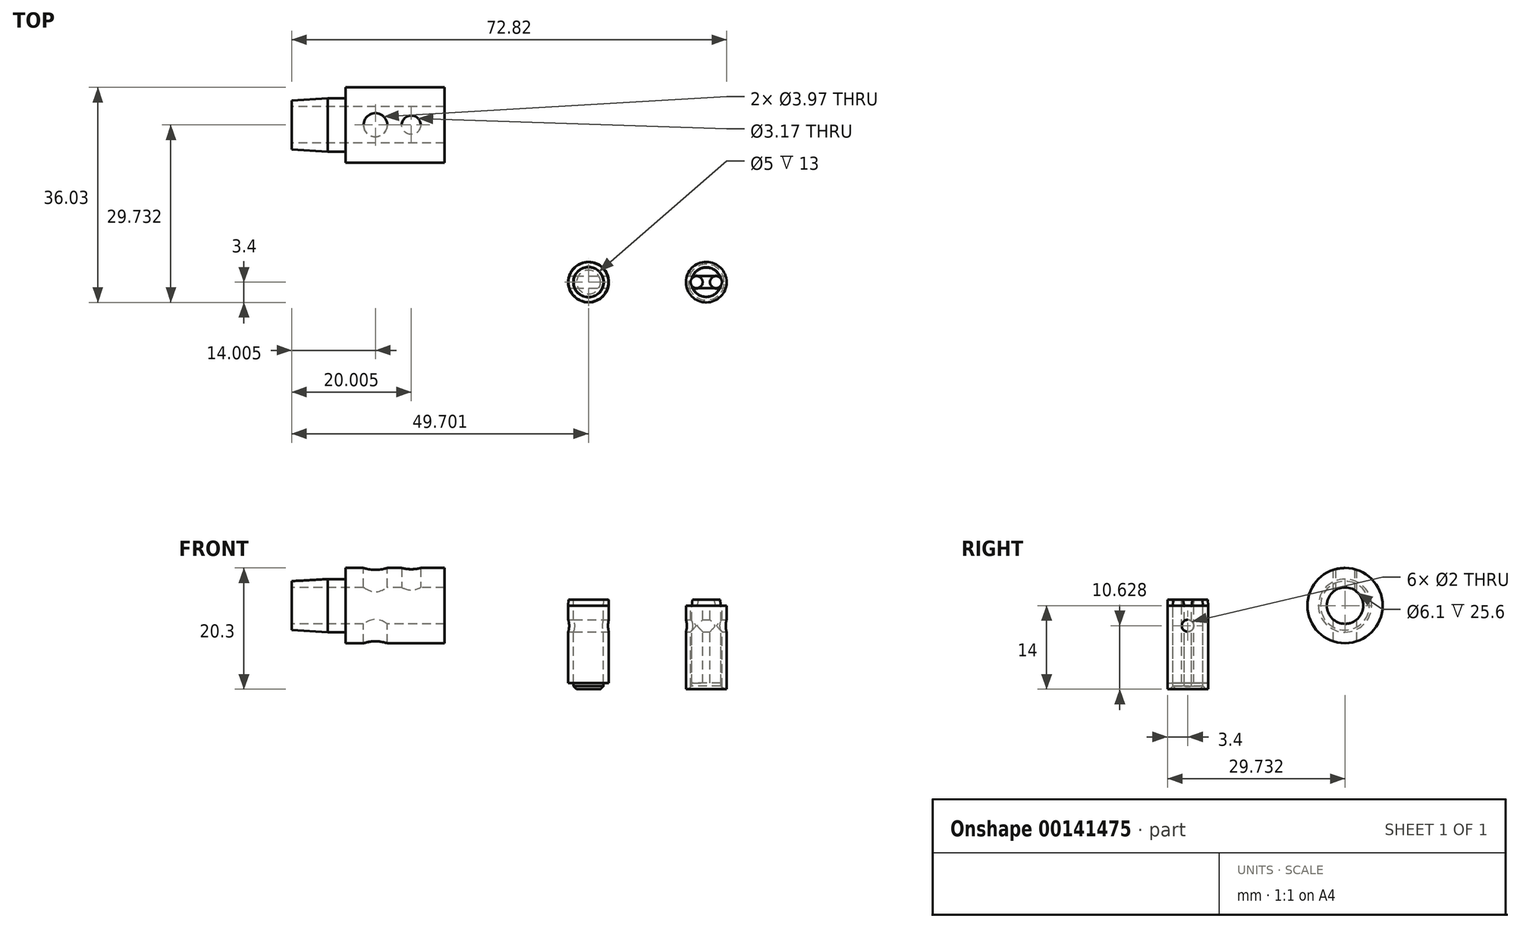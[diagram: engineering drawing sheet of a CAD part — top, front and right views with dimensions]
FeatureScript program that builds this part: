
annotation { "Feature Type Name" : "Feature", "Feature Type Description" : "" }
export const myFeature = defineFeature(function(context is Context, id is Id, definition is map)
    precondition{}
    {
        {
            var Q0;
            Q0=qCreatedBy(makeId("Top.planeOp"),FACE);
            var sketch = newSketch(context, id + "F0", { "sketchPlane" : qUnion([Q0])});
            skCircle(sketch, "E0", {"center": v(0, 0) * mm, "radius": 3.4 * mm});
            skCircle(sketch, "E1", {"center": v(0, 0) * mm, "radius": 2.5 * mm});
            skLineSegment(sketch, "E2", {"start": v(-9.86, 9.58) * mm, "end": v(-9.86, -9.58) * mm, "construction": true});
            skCircle(sketch, "E3.MirrorC", {"center": v(-19.72, 0) * mm, "radius": 2.5 * mm});
            skCircle(sketch, "E4.MirrorC", {"center": v(-19.72, 0) * mm, "radius": 3.4 * mm});
            skCircle(sketch, "E5", {"center": v(1.62, 0) * mm, "radius": 1.01 * mm});
            skLineSegment(sketch, "E6", {"start": v(0, 0) * mm, "end": v(0, 2.5) * mm, "construction": true});
            skCircle(sketch, "E7.MirrorC", {"center": v(-1.62, 0) * mm, "radius": 1.01 * mm});
            skLineSegment(sketch, "E8", {"start": v(-1.62, 1.01) * mm, "end": v(1.62, 1.01) * mm});
            skLineSegment(sketch, "E9", {"start": v(1.62, 1.01) * mm, "end": v(1.62, -1.01) * mm});
            skLineSegment(sketch, "E10", {"start": v(1.62, -1.01) * mm, "end": v(-1.62, -1.01) * mm});
            skLineSegment(sketch, "E11", {"start": v(-1.62, -1.01) * mm, "end": v(-1.62, 1.01) * mm});
            skCircle(sketch, "E12.MirrorC", {"center": v(-21.34, 0) * mm, "radius": 1.01 * mm});
            skSolve(sketch);
        }
        {
            var Q0;
            Q0=makeQuery(id+"F0.imprint","IMPRINT",FACE,{"disambiguationData":[TD([[makeQuery(id+"F0.imprint","IMPRINT",EDGE,{"derivedFrom":sQuery(id+"F0.wireOp",EDGE,"E0")}),1.0]])]});
            var Q1;
            Q1=makeQuery(id+"F0.imprint","IMPRINT",FACE,{"disambiguationData":[TD([[makeQuery(id+"F0.imprint","IMPRINT",EDGE,{"derivedFrom":sQuery(id+"F0.wireOp",EDGE,"E3.MirrorC")}),1.0]])]});
            var Q2;
            Q2=sQuery(id+"F0.wireOp",EDGE,"E0");
            extrude(context, id + "F1", {"entities" : qUnion([Q0, Q1]), "surfaceEntities" : qUnion([Q2]), "oppositeDirection" : true, "depth" : 14 * mm});
        }
        {
            var Q0;
            {var subQ0=sQuery(id+"F0.wireOp",EDGE,"E11");Q0=makeQuery(id+"F0.imprint","IMPRINT",FACE,{"disambiguationData":[TD([[makeQuery(id+"F0.imprint","IMPRINT",EDGE,{"derivedFrom":subQ0}),-1.0]])]});}
            var Q1;
            {var subQ4=sQuery(id+"F0.wireOp",EDGE,"E11");Q1=makeQuery(id+"F0.imprint","IMPRINT",FACE,{"disambiguationData":[TD([[makeQuery(id+"F0.imprint","IMPRINT",EDGE,{"derivedFrom":subQ4}),1.0]])]});}
            var Q2;
            {var subQ0=sQuery(id+"F0.wireOp",EDGE,"E9");Q2=makeQuery(id+"F0.imprint","IMPRINT",FACE,{"disambiguationData":[TD([[makeQuery(id+"F0.imprint","IMPRINT",EDGE,{"derivedFrom":subQ0}),-1.0]])]});}
            var Q3;
            {var subQ4=sQuery(id+"F0.wireOp",EDGE,"E9");Q3=makeQuery(id+"F0.imprint","IMPRINT",FACE,{"disambiguationData":[TD([[makeQuery(id+"F0.imprint","IMPRINT",EDGE,{"derivedFrom":subQ4}),1.0]])]});}
            extrude(context, id + "F2", {"entities" : qUnion([Q0, Q1, Q2, Q3]), "operationType" : NewBodyOperationType.REMOVE, "oppositeDirection" : true, "depth" : 15 * mm, "hasSecondDirection" : true, "secondDirectionOppositeDirection" : false, "secondDirectionDepth" : 5 * mm});
        }
        {
            var Q0;
            {var subQ5=sQuery(id+"F0.wireOp",EDGE,"E8");Q0=makeQuery(id+"F0.imprint","IMPRINT",FACE,{"disambiguationData":[TD([[makeQuery(id+"F0.imprint","IMPRINT",EDGE,{"derivedFrom":subQ5}),1.0]])]});}
            var Q1;
            {var subQ5=sQuery(id+"F0.wireOp",EDGE,"E10");Q1=makeQuery(id+"F0.imprint","IMPRINT",FACE,{"disambiguationData":[TD([[makeQuery(id+"F0.imprint","IMPRINT",EDGE,{"derivedFrom":subQ5}),1.0]])]});}
            var Q2;
            {var subQ0=sQuery(id+"F0.wireOp",EDGE,"E12.MirrorC");var subQ1=sQuery(id+"F0.wireOp",EDGE,"E3.MirrorC");var subQ2=makeQuery(id+"F0.imprint","INTERSECT",VERTEX,{"disambiguationData":[OD(0.0)],"derivedFrom":[subQ1,subQ0]});Q2=makeQuery(id+"F0.imprint","IMPRINT",FACE,{"disambiguationData":[TD([[makeQuery(id+"F0.imprint","IMPRINT",EDGE,{"disambiguationData":[TD([[subQ2,1.0]])],"derivedFrom":subQ1}),-1.0]])]});}
            var Q3;
            {var subQ0=sQuery(id+"F0.wireOp",EDGE,"E12.MirrorC");var subQ1=sQuery(id+"F0.wireOp",EDGE,"E3.MirrorC");var subQ2=makeQuery(id+"F0.imprint","INTERSECT",VERTEX,{"disambiguationData":[OD(0.0)],"derivedFrom":[subQ1,subQ0]});Q3=makeQuery(id+"F0.imprint","IMPRINT",FACE,{"disambiguationData":[TD([[makeQuery(id+"F0.imprint","IMPRINT",EDGE,{"disambiguationData":[TD([[subQ2,-1.0]])],"derivedFrom":subQ1}),-1.0]])]});}
            var Q4;
            {var subQ1=sQuery(id+"F0.wireOp",EDGE,"E8");Q4=makeQuery(id+"F0.imprint","IMPRINT",FACE,{"disambiguationData":[TD([[makeQuery(id+"F0.imprint","IMPRINT",EDGE,{"derivedFrom":subQ1}),-1.0]])]});}
            var Q5;
            Q5=sQuery(id+"F0.wireOp",EDGE,"E1");
            var Q6;
            Q6=makeQuery(id+"F1.opExtrude","CAP_FACE",FACE,{"disambiguationData":[OSD([sQuery(id+"F0.wireOp",EDGE,"E3.MirrorC"),sQuery(id+"F0.wireOp",EDGE,"E4.MirrorC")])],"isStart":false});
            extrude(context, id + "F3", {"entities" : qUnion([Q0, Q1, Q2, Q3, Q4]), "surfaceEntities" : qUnion([Q5]), "oppositeDirection" : true, "endBoundEntityFace" : qUnion([Q6]), "depth" : 13 * mm, "hasSecondDirection" : true, "secondDirectionOppositeDirection" : false, "secondDirectionDepth" : 1 * mm, "hasSecondDirectionDraft" : true, "secondDirectionDraftAngle" : 3 * degree, "secondDirectionDraftPullDirection" : true});
        }
        {
            var Q0;
            {var subQ0=sQuery(id+"F0.wireOp",EDGE,"E8");var subQ1=sQuery(id+"F0.wireOp",EDGE,"E5");var subQ2=makeQuery(id+"F0.imprint","INTERSECT",VERTEX,{"derivedFrom":[subQ1,subQ0]});Q0=makeQuery(id+"F0.imprint","IMPRINT",FACE,{"disambiguationData":[TD([[makeQuery(id+"F0.imprint","IMPRINT",EDGE,{"disambiguationData":[TD([[subQ2,-1.0]])],"derivedFrom":subQ1}),-1.0]])]});}
            extrude(context, id + "F4", {"entities" : qUnion([Q0]), "operationType" : NewBodyOperationType.REMOVE, "depth" : 2 * mm});
        }
        {
            var Q0;
            Q0=makeQuery(id+"F1.opExtrude","CAP_EDGE",EDGE,{"disambiguationData":[OSD([sQuery(id+"F0.wireOp",EDGE,"E1")])],"isStart":false});
            var Q1;
            Q1=makeQuery(id+"F1.opExtrude","CAP_EDGE",EDGE,{"disambiguationData":[OSD([sQuery(id+"F0.wireOp",EDGE,"E3.MirrorC")])],"isStart":false});
            chamfer(context, id + "F5", {"entities" : qUnion([Q0, Q1]), "width" : .5 * mm, "tangentPropagation" : true});
        }
        {
            var Q0;
            Q0=qCreatedBy(makeId("Right.planeOp"),FACE);
            cPlane(context, id + "F6", {"entities" : qUnion([Q0]), "cplaneType" : CPlaneType.OFFSET, "offset" : 25 * mm, "width" : 150 * mm, "height" : 150 * mm});
        }
        {
            var Q0;
            Q0=qCreatedBy(id+"F6.planeOp",FACE);
            var sketch = newSketch(context, id + "F7", { "sketchPlane" : qUnion([Q0])});
            skCircle(sketch, "E13", {"center": v(0, -3.37) * mm, "radius": 1 * mm});
            skSolve(sketch);
        }
        {
            var Q0;
            Q0 = qSketchRegion(id + "F7", true);
            extrude(context, id + "F8", {"entities" : qUnion([Q0]), "operationType" : NewBodyOperationType.REMOVE, "oppositeDirection" : true, "depth" : 100 * mm});
        }
        {
            var Q0;
            Q0=qCreatedBy(makeId("Top.planeOp"),FACE);
            var sketch = newSketch(context, id + "F9", { "sketchPlane" : qUnion([Q0])});
            skLineSegment(sketch, "E14", {"start": v(-55.42, 26.33) * mm, "end": v(-48.93, 26.33) * mm, "construction": true});
            skLineSegment(sketch, "E15", {"start": v(-60.42, 30.78) * mm, "end": v(-60.42, 32.63) * mm});
            skLineSegment(sketch, "E16", {"start": v(-60.42, 32.63) * mm, "end": v(-43.82, 32.63) * mm});
            skLineSegment(sketch, "E17", {"start": v(-69.42, 29.38) * mm, "end": v(-43.82, 29.38) * mm});
            skCircle(sketch, "E18", {"center": v(-49.42, 26.33) * mm, "radius": 1.59 * mm});
            skCircle(sketch, "E19", {"center": v(-55.42, 26.33) * mm, "radius": 1.98 * mm});
            skLineSegment(sketch, "E20", {"start": v(-55.42, 26.33) * mm, "end": v(-77.02, 26.33) * mm});
            skPoint(sketch, "E21", {"position": v(-63.42, 30.78) * mm});
            skCircle(sketch, "E22", {"center": v(-49.42, 26.33) * mm, "radius": 1.98 * mm});
            skLineSegment(sketch, "E23", {"start": v(-69.42, 30.43) * mm, "end": v(-69.42, 29.38) * mm});
            skLineSegment(sketch, "E24", {"start": v(-43.82, 32.63) * mm, "end": v(-43.82, 29.38) * mm});
            skLineSegment(sketch, "E25", {"start": v(-63.42, 30.78) * mm, "end": v(-60.42, 30.78) * mm});
            skLineSegment(sketch, "E26", {"start": v(-69.42, 30.43) * mm, "end": v(-63.42, 30.78) * mm});
            skLineSegment(sketch, "E27.MirrorCS", {"start": v(-69.42, 23.28) * mm, "end": v(-43.82, 23.28) * mm});
            skLineSegment(sketch, "E28.MirrorCS", {"start": v(-60.42, 20.03) * mm, "end": v(-43.82, 20.03) * mm});
            skLineSegment(sketch, "E29.MirrorCS", {"start": v(-43.82, 20.03) * mm, "end": v(-43.82, 23.28) * mm});
            skLineSegment(sketch, "E30.MirrorCS", {"start": v(-60.42, 21.88) * mm, "end": v(-60.42, 20.03) * mm});
            skLineSegment(sketch, "E31.MirrorCS", {"start": v(-63.42, 21.88) * mm, "end": v(-60.42, 21.88) * mm});
            skLineSegment(sketch, "E32.MirrorCS", {"start": v(-69.42, 22.24) * mm, "end": v(-63.42, 21.88) * mm});
            skLineSegment(sketch, "E33.MirrorCS", {"start": v(-69.42, 22.24) * mm, "end": v(-69.42, 23.28) * mm});
            skSolve(sketch);
        }
        {
            var Q0;
            Q0=makeQuery(id+"F9.imprint","IMPRINT",FACE,{"disambiguationData":[TD([[makeQuery(id+"F9.imprint","IMPRINT",EDGE,{"derivedFrom":sQuery(id+"F9.wireOp",EDGE,"E15")}),-1.0]])]});
            var Q1;
            Q1=sQuery(id+"F9.wireOp",EDGE,"E14");
            revolve(context, id + "F10", {"entities" : qUnion([Q0]), "axis" : qUnion([Q1]), "revolveType" : RevolveType.FULL});
        }
        {
            var Q0;
            Q0=makeQuery(id+"F9.imprint","IMPRINT",FACE,{"disambiguationData":[TD([[makeQuery(id+"F9.imprint","IMPRINT",EDGE,{"derivedFrom":sQuery(id+"F9.wireOp",EDGE,"E19")}),1.0]])]});
            extrude(context, id + "F11", {"entities" : qUnion([Q0]), "operationType" : NewBodyOperationType.REMOVE, "oppositeDirection" : true, "depth" : 25 * mm, "hasSecondDirection" : true, "secondDirectionOppositeDirection" : false, "secondDirectionDepth" : 25 * mm});
        }
        {
            var Q0;
            Q0=makeQuery(id+"F9.imprint","IMPRINT",FACE,{"disambiguationData":[TD([[makeQuery(id+"F9.imprint","IMPRINT",EDGE,{"derivedFrom":sQuery(id+"F9.wireOp",EDGE,"E18")}),1.0]])]});
            extrude(context, id + "F12", {"entities" : qUnion([Q0]), "operationType" : NewBodyOperationType.REMOVE, "depth" : 9 * mm});
        }
    });
